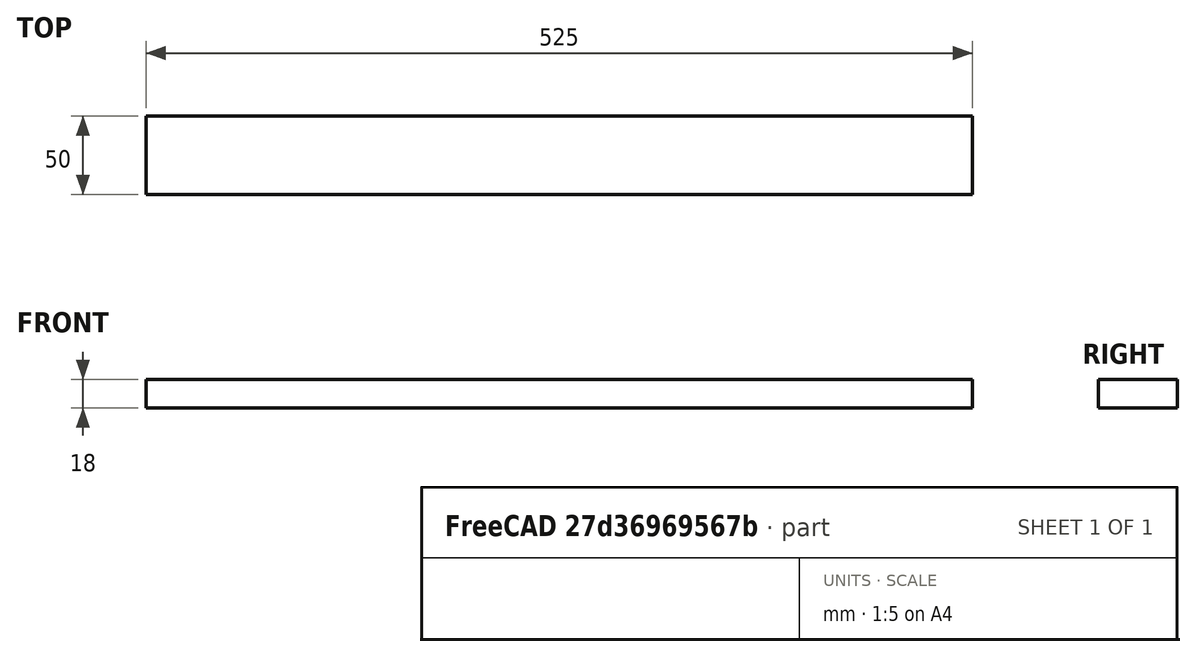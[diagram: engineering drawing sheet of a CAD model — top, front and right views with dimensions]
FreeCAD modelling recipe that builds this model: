
FCSTD DOCUMENT  (FreeCAD 1.0R39109 (Git))
Label: 81_base_front_and_back
License: All rights reserved
LicenseURL: http://en.wikipedia.org/wiki/All_rights_reserved
objects: Spreadsheet::Sheet×1, Sketcher::SketchObject×1, PartDesign::Pad×1, PartDesign::Body×1
note: 6 computed .brp shape members not serialized (recipe doc carries the construction recipe); baked Part::Feature solids carry a one-line shape summary decoded from their .brp

FEATURE [Spreadsheet::Sheet] Spreadsheet
  cells = A2='length; B2(length)=525; A3='width; B3(width)=50; A4='height; B4(height)=18
FEATURE [Sketcher::SketchObject] Sketch
  ArcFitTolerance = 0
  AttachmentSupport = -> [XY_Plane]
  FullyConstrained = true
  MakeInternals = false
  MapMode = 5
  expr: Constraints[11] = Spreadsheet.length
  expr: Constraints[12] = Spreadsheet.width
  sketch-geometry (5):
    g0: LineSegment StartX=-262.5 StartY=25 StartZ=0 EndX=262.5 EndY=25 EndZ=0
    g1: LineSegment StartX=262.5 StartY=25 StartZ=0 EndX=262.5 EndY=-25 EndZ=0
    g2: LineSegment StartX=262.5 StartY=-25 StartZ=0 EndX=-262.5 EndY=-25 EndZ=0
    g3: LineSegment StartX=-262.5 StartY=-25 StartZ=0 EndX=-262.5 EndY=25 EndZ=0
    g4: LineSegment [constr] StartX=-262.5 StartY=25 StartZ=0 EndX=262.5 EndY=-25 EndZ=0
  constraints (13):
    c: Coincident(g0,g1)
    c: Coincident(g1,g2)
    c: Coincident(g2,g3)
    c: Coincident(g3,g0)
    c: Horizontal(g0)
    c: Horizontal(g2)
    c: Vertical(g1)
    c: Vertical(g3)
    c: Coincident(g4,g1)
    c: Coincident(g0,g4)
    c: Symmetric(g0,g1,g-1)
    c: Distance(g0,g0) = 525
    c: Distance(g0,g2) = 50
FEATURE [PartDesign::Pad] Pad
  Direction = (0,0,1)
  Length = 18
  Length2 = 10
  Profile = -> Sketch
  ReferenceAxis = -> Sketch [N_Axis]
  Suppressed = false
  Type = 0
  expr: Length = Spreadsheet.height
FEATURE [PartDesign::Body] Body
  AllowCompound = false
  Group = -> [Sketch,Pad]
  Origin = -> Origin
  Tip = -> Pad
